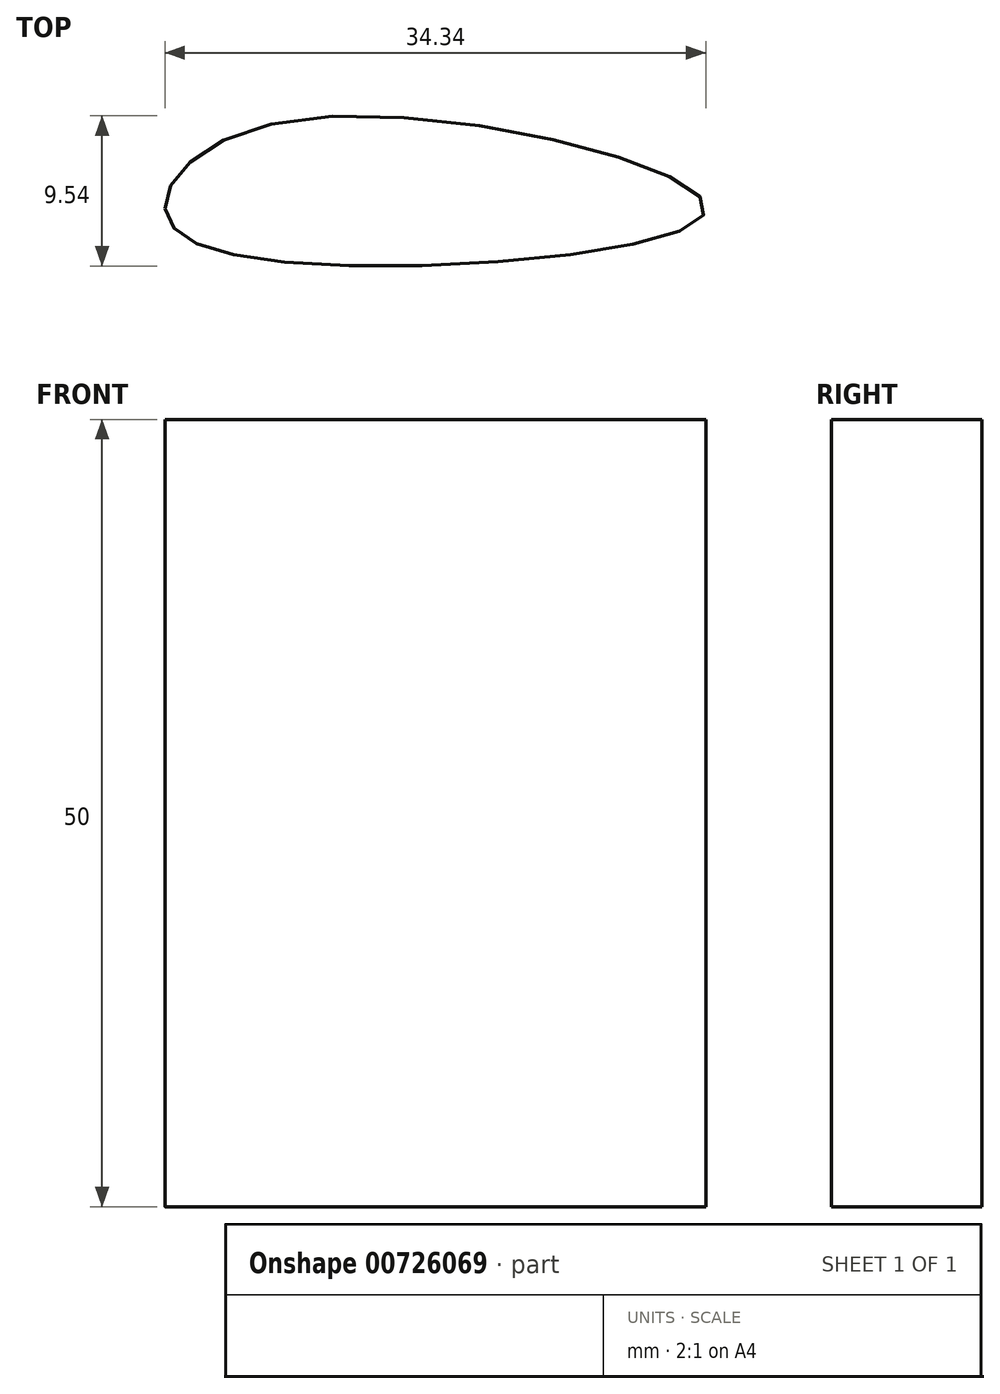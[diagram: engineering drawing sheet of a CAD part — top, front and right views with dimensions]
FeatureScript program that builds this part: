
annotation { "Feature Type Name" : "Feature", "Feature Type Description" : "" }
export const myFeature = defineFeature(function(context is Context, id is Id, definition is map)
    precondition{}
    {
        {
            var Q0;
            Q0=qCreatedBy(makeId("Top.planeOp"),FACE);
            var sketch = newSketch(context, id + "F0", { "sketchPlane" : qUnion([Q0])});
            skFitSpline(sketch, "E0", {"points": [v(-8.32, 0) * mm, v(0, 5.65) * mm, v(26, 0) * mm, v(0, -3.46) * mm, v(-8.32, 0) * mm]});
            skSolve(sketch);
        }
        {
            var Q0;
            Q0 = qSketchRegion(id + "F0", true);
            extrude(context, id + "F1", {"entities" : qUnion([Q0]), "depth" : 50 * mm, "offsetDistance" : 25 * mm});
        }
    });
